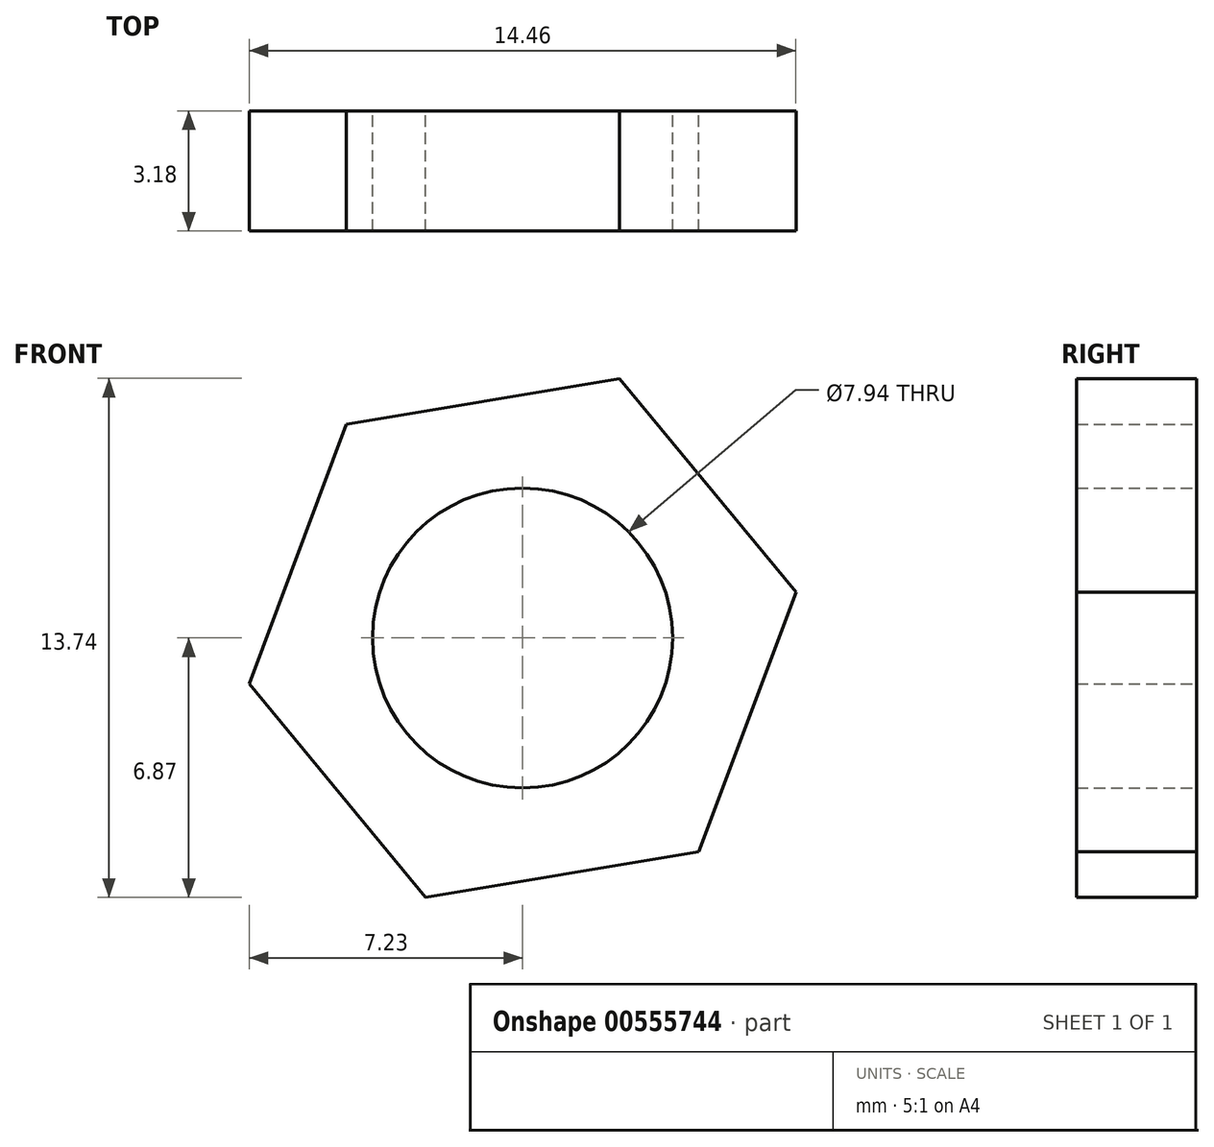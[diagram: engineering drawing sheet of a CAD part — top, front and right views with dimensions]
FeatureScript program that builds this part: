
annotation { "Feature Type Name" : "Feature", "Feature Type Description" : "" }
export const myFeature = defineFeature(function(context is Context, id is Id, definition is map)
    precondition{}
    {
        {
            var Q0;
            Q0=qCreatedBy(makeId("Front.planeOp"),FACE);
            var sketch = newSketch(context, id + "F0", { "sketchPlane" : qUnion([Q0])});
            skCircle(sketch, "E0.cCircle", {"center": v(0, 0) * mm, "radius": 6.35 * mm, "construction": true});
            skLineSegment(sketch, "E0.0", {"start": v(-2.57, -6.87) * mm, "end": v(-7.23, -1.2) * mm});
            skLineSegment(sketch, "E0.1", {"start": v(-7.23, -1.2) * mm, "end": v(-4.66, 5.66) * mm});
            skLineSegment(sketch, "E0.2", {"start": v(-4.66, 5.66) * mm, "end": v(2.57, 6.87) * mm});
            skLineSegment(sketch, "E0.3", {"start": v(2.57, 6.87) * mm, "end": v(7.23, 1.2) * mm});
            skLineSegment(sketch, "E0.4", {"start": v(7.23, 1.2) * mm, "end": v(4.66, -5.66) * mm});
            skLineSegment(sketch, "E0.5", {"start": v(4.66, -5.66) * mm, "end": v(-2.57, -6.87) * mm});
            skPoint(sketch, "E0.0.midPoint", {"position": v(-4.9, -4.04) * mm});
            skCircle(sketch, "E1", {"center": v(0, 0) * mm, "radius": 3.97 * mm});
            skSolve(sketch);
        }
        {
            var Q0;
            Q0=makeQuery(id+"F0.imprint","IMPRINT",FACE,{"disambiguationData":[TD([[makeQuery(id+"F0.imprint","IMPRINT",EDGE,{"derivedFrom":sQuery(id+"F0.wireOp",EDGE,"E0.0")}),-1.0]])]});
            extrude(context, id + "F1", {"entities" : qUnion([Q0]), "depth" : 3.17 * mm, "offsetDistance" : 25.4 * mm});
        }
    });
